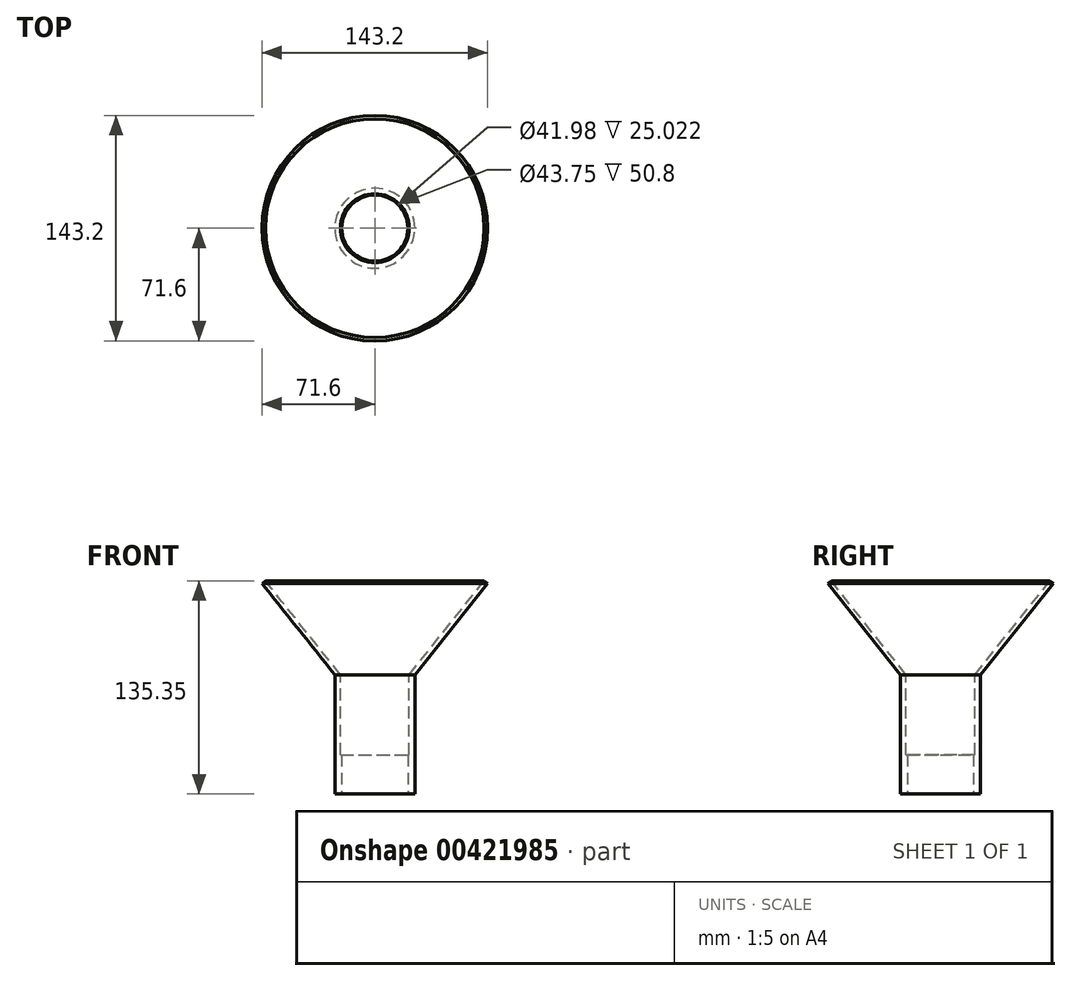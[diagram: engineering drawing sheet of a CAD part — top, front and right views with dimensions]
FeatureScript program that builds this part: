
annotation { "Feature Type Name" : "Feature", "Feature Type Description" : "" }
export const myFeature = defineFeature(function(context is Context, id is Id, definition is map)
    precondition{}
    {
        {
            var Q0;
            Q0=qCreatedBy(makeId("Front.planeOp"),FACE);
            var sketch = newSketch(context, id + "F0", { "sketchPlane" : qUnion([Q0])});
            skLineSegment(sketch, "E0", {"start": v(0, 0) * mm, "end": v(0, -75.82) * mm});
            skLineSegment(sketch, "E1", {"start": v(0, -75.82) * mm, "end": v(-25.4, -75.82) * mm});
            skLineSegment(sketch, "E2", {"start": v(-25.4, -75.82) * mm, "end": v(-25.4, 0) * mm});
            skLineSegment(sketch, "E3", {"start": v(-25.4, 0) * mm, "end": v(-3.53, 0) * mm});
            skLineSegment(sketch, "E4", {"start": v(-3.53, 0) * mm, "end": v(44.03, 59.53) * mm});
            skLineSegment(sketch, "E5", {"start": v(44.03, 59.53) * mm, "end": v(46.2, 57.8) * mm});
            skLineSegment(sketch, "E6", {"start": v(46.2, 57.8) * mm, "end": v(0, 0) * mm});
            skSolve(sketch);
        }
        {
            var Q0;
            Q0=makeQuery(id+"F0.imprint","IMPRINT",FACE,{"disambiguationData":[TD([[makeQuery(id+"F0.imprint","IMPRINT",EDGE,{"derivedFrom":sQuery(id+"F0.wireOp",EDGE,"E0")}),-1.0]])]});
            var Q1;
            Q1=sQuery(id+"F0.wireOp",EDGE,"E2");
            revolve(context, id + "F1", {"entities" : qUnion([Q0]), "axis" : qUnion([Q1]), "revolveType" : RevolveType.FULL});
        }
        {
            var Q0;
            Q0=makeQuery(id+"F1.opRevolve","SWEPT_FACE",FACE,{"disambiguationData":[OSD([sQuery(id+"F0.wireOp",EDGE,"E1")])]});
            var sketch = newSketch(context, id + "F2", { "sketchPlane" : qUnion([Q0])});
            skCircle(sketch, "E7", {"center": v(-25.4, 0) * mm, "radius": 21 * mm});
            skSolve(sketch);
        }
        {
            var Q0;
            Q0=makeQuery(id+"F2.imprint","IMPRINT",FACE,{"disambiguationData":[TD([[makeQuery(id+"F2.imprint","IMPRINT",EDGE,{"derivedFrom":sQuery(id+"F2.wireOp",EDGE,"E7")}),1.0]])]});
            extrude(context, id + "F3", {"entities" : qUnion([Q0]), "operationType" : NewBodyOperationType.REMOVE, "oppositeDirection" : true, "depth" : 25.4 * mm});
        }
        {
            var Q0;
            Q0=makeQuery(id+"F1.opRevolve","SWEPT_FACE",FACE,{"disambiguationData":[OSD([sQuery(id+"F0.wireOp",EDGE,"E3")])]});
            extrude(context, id + "F4", {"entities" : qUnion([Q0]), "operationType" : NewBodyOperationType.REMOVE, "oppositeDirection" : true, "depth" : 25.4 * mm});
        }
        {
            var Q0;
            Q0=makeQuery(id+"F4.boolean.opBoolean","COPY",FACE,{"derivedFrom":makeQuery(id+"F4.opExtrude","CAP_FACE",FACE,{"disambiguationData":[OSD([sQuery(id+"F0.wireOp",EDGE,"E3")])],"isStart":false})});
            extrude(context, id + "F5", {"entities" : qUnion([Q0]), "operationType" : NewBodyOperationType.REMOVE, "oppositeDirection" : true, "depth" : 25.4 * mm});
        }
    });
